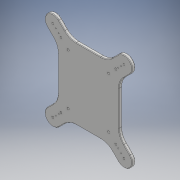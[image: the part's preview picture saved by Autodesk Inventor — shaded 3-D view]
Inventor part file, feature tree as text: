
AUTODESK INVENTOR PART (.ipt)
format: ipt  version: 2018 (Build 220112000, 112)  size: 291,840 bytes
history: native  units: mm
features: fillet x2, extrude x1
ambient origin geometry x8: Origin, YZ Plane, XZ Plane, XY Plane, X Axis, Y Axis, Z Axis, Center Point
bodies: Body1 (feature_tree)
feature tree (3):
  extrude  "Extrusion4"  Depth=60.0mm
  fillet  "Fillet6"  Radius=70.0mm
  fillet  "Fillet7"  Radius=2.0mm
